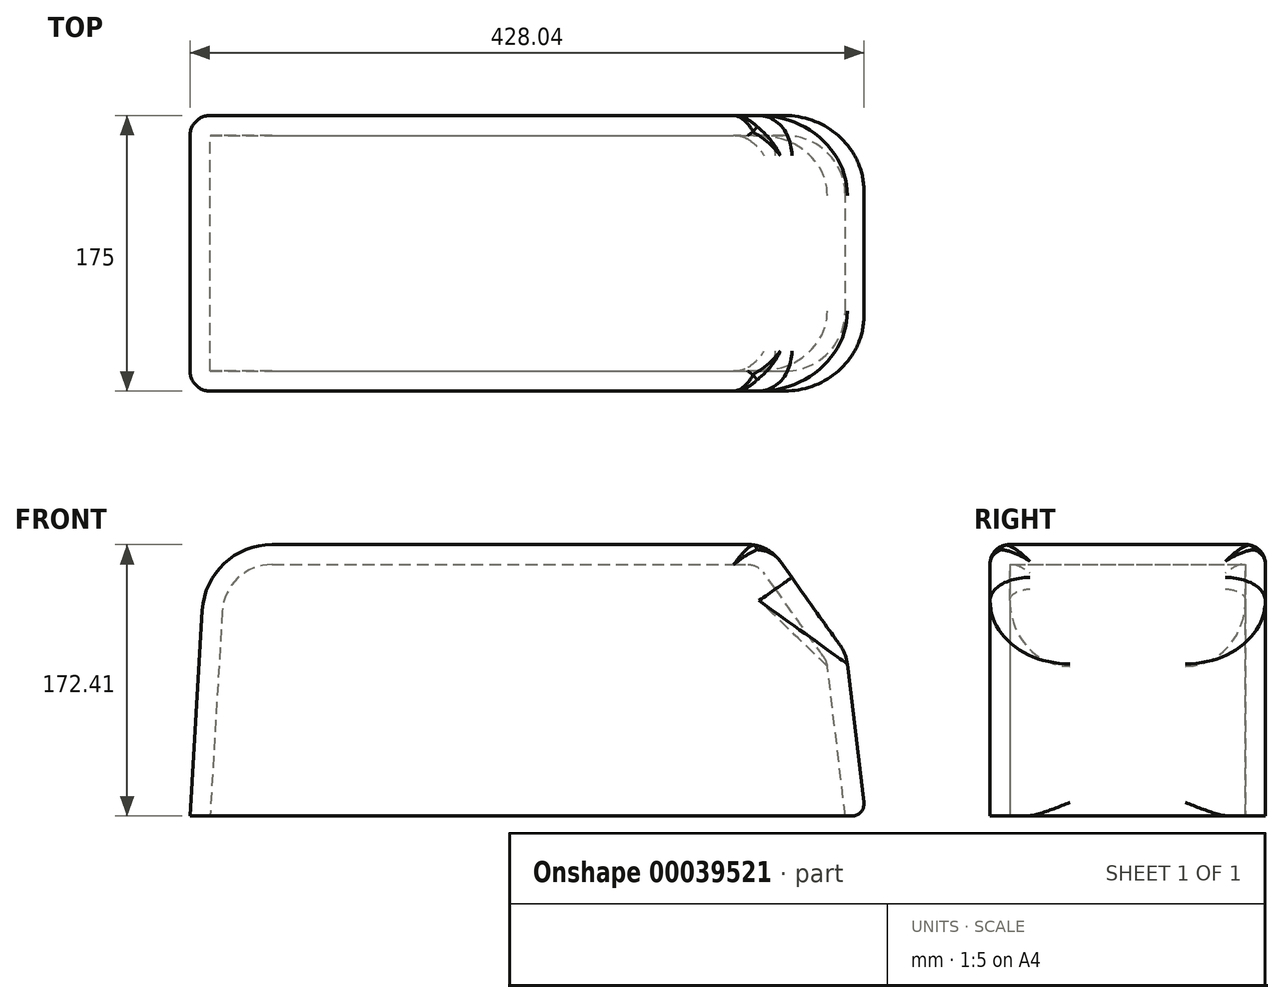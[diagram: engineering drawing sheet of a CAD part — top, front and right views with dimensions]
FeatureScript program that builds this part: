
annotation { "Feature Type Name" : "Feature", "Feature Type Description" : "" }
export const myFeature = defineFeature(function(context is Context, id is Id, definition is map)
    precondition{}
    {
        {
            var Q0;
            Q0=qCreatedBy(makeId("Front.planeOp"),FACE);
            var sketch = newSketch(context, id + "F0", { "sketchPlane" : qUnion([Q0])});
            skPoint(sketch, "E0", {"position": v(0, 0) * mm});
            skPoint(sketch, "E1", {"position": v(-144.5, 0) * mm});
            skPoint(sketch, "E2", {"position": v(95.54, 0) * mm});
            skPoint(sketch, "E3", {"position": v(-169.9, 0) * mm});
            skPoint(sketch, "E4", {"position": v(-119.1, 0) * mm});
            skPoint(sketch, "E5", {"position": v(70.14, 0) * mm});
            skPoint(sketch, "E6", {"position": v(120.94, 0) * mm});
            skLineSegment(sketch, "E7", {"start": v(-213.07, 0) * mm, "end": v(-205.3, 130.6) * mm});
            skLineSegment(sketch, "E8", {"start": v(-213.07, 0) * mm, "end": v(-169.9, 0) * mm});
            skLineSegment(sketch, "E9", {"start": v(-119.1, 0) * mm, "end": v(70.14, 0) * mm});
            skLineSegment(sketch, "E10", {"start": v(120.94, 0) * mm, "end": v(207.35, 0) * mm});
            skPoint(sketch, "E11", {"position": v(168.44, 0) * mm});
            skLineSegment(sketch, "E12", {"start": v(214.92, 8.52) * mm, "end": v(204.41, 96.5) * mm});
            skLineSegment(sketch, "E13", {"start": v(199.9, 108.2) * mm, "end": v(161.88, 161.72) * mm});
            skLineSegment(sketch, "E14", {"start": v(-160.93, 172.41) * mm, "end": v(141.18, 172.41) * mm});
            skPoint(sketch, "E15.visualSharp", {"position": v(-202.81, 172.41) * mm});
            skArc(sketch, "E15.filletArc", {"start": v(-160.93, 172.41) * mm, "mid": v(-191.41, 160.32) * mm, "end": v(-205.3, 130.6) * mm});
            skPoint(sketch, "E16.visualSharp", {"position": v(215.93, 0) * mm});
            skArc(sketch, "E16.filletArc", {"start": v(207.35, 0) * mm, "mid": v(213.05, 2.56) * mm, "end": v(214.92, 8.52) * mm});
            skPoint(sketch, "E17.visualSharp", {"position": v(203.64, 102.93) * mm});
            skArc(sketch, "E17.filletArc", {"start": v(204.41, 96.5) * mm, "mid": v(202.89, 102.64) * mm, "end": v(199.9, 108.2) * mm});
            skPoint(sketch, "E18.visualSharp", {"position": v(154.29, 172.41) * mm});
            skArc(sketch, "E18.filletArc", {"start": v(161.88, 161.72) * mm, "mid": v(152.83, 169.58) * mm, "end": v(141.18, 172.41) * mm});
            skLineSegment(sketch, "E19", {"start": v(-169.9, 0) * mm, "end": v(-119.1, 0) * mm});
            skLineSegment(sketch, "E20", {"start": v(70.14, 0) * mm, "end": v(120.94, 0) * mm});
            skSolve(sketch);
        }
        {
            var Q0;
            Q0=makeQuery(id+"F0.imprint","IMPRINT",FACE,{"disambiguationData":[TD([[makeQuery(id+"F0.imprint","IMPRINT",EDGE,{"derivedFrom":sQuery(id+"F0.wireOp",EDGE,"E7")}),-1.0]])]});
            extrude(context, id + "F1", {"entities" : qUnion([Q0]), "endBound" : BoundingType.SYMMETRIC, "depth" : 175 * mm});
        }
        {
            var Q0;
            Q0=makeQuery(id+"F1.opExtrude","CAP_EDGE",EDGE,{"disambiguationData":[OSD([sQuery(id+"F0.wireOp",EDGE,"E7")])],"isStart":false});
            var Q1;
            Q1=makeQuery(id+"F1.opExtrude","CAP_EDGE",EDGE,{"disambiguationData":[OSD([sQuery(id+"F0.wireOp",EDGE,"E15.filletArc")])],"isStart":false});
            var Q2;
            Q2=makeQuery(id+"F1.opExtrude","CAP_EDGE",EDGE,{"disambiguationData":[OSD([sQuery(id+"F0.wireOp",EDGE,"E14")])],"isStart":false});
            var Q3;
            Q3=makeQuery(id+"F1.opExtrude","CAP_EDGE",EDGE,{"disambiguationData":[OSD([sQuery(id+"F0.wireOp",EDGE,"E14")])],"isStart":true});
            var Q4;
            Q4=makeQuery(id+"F1.opExtrude","CAP_EDGE",EDGE,{"disambiguationData":[OSD([sQuery(id+"F0.wireOp",EDGE,"E15.filletArc")])],"isStart":true});
            var Q5;
            Q5=makeQuery(id+"F1.opExtrude","CAP_EDGE",EDGE,{"disambiguationData":[OSD([sQuery(id+"F0.wireOp",EDGE,"E7")])],"isStart":true});
            fillet(context, id + "F2", {"entities" : qUnion([Q0, Q1, Q2, Q3, Q4, Q5]), "radius" : 12.7 * mm, "allowEdgeOverflow" : false});
        }
        {
            var Q0;
            Q0=makeQuery(id+"F1.opExtrude","CAP_EDGE",EDGE,{"disambiguationData":[OSD([sQuery(id+"F0.wireOp",EDGE,"E12")])],"isStart":false});
            var Q1;
            Q1=makeQuery(id+"F1.opExtrude","CAP_EDGE",EDGE,{"disambiguationData":[OSD([sQuery(id+"F0.wireOp",EDGE,"E12")])],"isStart":true});
            fillet(context, id + "F3", {"entities" : qUnion([Q0, Q1]), "radius" : 50.8 * mm, "allowEdgeOverflow" : false});
        }
        {
            var Q0;
            Q0=makeQuery(id+"F3.opFillet","BLEND_EDGE",EDGE,{"blendedFrom":[makeQuery(id+"F1.opExtrude","CAP_EDGE",EDGE,{"disambiguationData":[OSD([sQuery(id+"F0.wireOp",EDGE,"E12")])],"isStart":false}),makeQuery(id+"F1.opExtrude","SWEPT_FACE",FACE,{"disambiguationData":[OSD([sQuery(id+"F0.wireOp",EDGE,"E13")])]})],"blendedInto":[makeQuery(id+"F1.opExtrude","SWEPT_FACE",FACE,{"disambiguationData":[OSD([sQuery(id+"F0.wireOp",EDGE,"E13")])]})]});
            var Q1;
            Q1=makeQuery(id+"F3.opFillet","BLEND_EDGE",EDGE,{"blendedFrom":[makeQuery(id+"F1.opExtrude","CAP_EDGE",EDGE,{"disambiguationData":[OSD([sQuery(id+"F0.wireOp",EDGE,"E12")])],"isStart":true}),makeQuery(id+"F1.opExtrude","SWEPT_FACE",FACE,{"disambiguationData":[OSD([sQuery(id+"F0.wireOp",EDGE,"E13")])]})],"blendedInto":[makeQuery(id+"F1.opExtrude","SWEPT_FACE",FACE,{"disambiguationData":[OSD([sQuery(id+"F0.wireOp",EDGE,"E13")])]})]});
            fillet(context, id + "F4", {"entities" : qUnion([Q0, Q1]), "radius" : 25.4 * mm, "allowEdgeOverflow" : false});
        }
        {
            var Q0;
            {var subQ0=sQuery(id+"F0.wireOp",EDGE,"E14");Q0=makeQuery(id+"F4.opFillet","BLEND_EDGE",EDGE,{"blendedFrom":[makeQuery(id+"F3.opFillet","BLEND_EDGE",EDGE,{"blendedFrom":[makeQuery(id+"F1.opExtrude","CAP_EDGE",EDGE,{"disambiguationData":[OSD([sQuery(id+"F0.wireOp",EDGE,"E12")])],"isStart":false}),makeQuery(id+"F1.opExtrude","SWEPT_FACE",FACE,{"disambiguationData":[OSD([sQuery(id+"F0.wireOp",EDGE,"E13")])]})],"blendedInto":[makeQuery(id+"F1.opExtrude","SWEPT_FACE",FACE,{"disambiguationData":[OSD([sQuery(id+"F0.wireOp",EDGE,"E13")])]})]}),makeQuery(id+"F2.opFillet","BLEND_FACE",FACE,{"disambiguationData":[OSD([subQ0]),TDD([makeQuery(id+"F1.opExtrude","CAP_EDGE",EDGE,{"disambiguationData":[OSD([subQ0])],"isStart":false})])]})],"blendedInto":[makeQuery(id+"F2.opFillet","BLEND_FACE",FACE,{"disambiguationData":[OSD([subQ0]),TDD([makeQuery(id+"F1.opExtrude","CAP_EDGE",EDGE,{"disambiguationData":[OSD([subQ0])],"isStart":false})])]})]});}
            var Q1;
            Q1=makeQuery(id+"F4.opFillet","BLEND_EDGE",EDGE,{"blendedFrom":[makeQuery(id+"F3.opFillet","BLEND_EDGE",EDGE,{"blendedFrom":[makeQuery(id+"F1.opExtrude","CAP_EDGE",EDGE,{"disambiguationData":[OSD([sQuery(id+"F0.wireOp",EDGE,"E12")])],"isStart":false}),makeQuery(id+"F1.opExtrude","SWEPT_FACE",FACE,{"disambiguationData":[OSD([sQuery(id+"F0.wireOp",EDGE,"E13")])]})],"blendedInto":[makeQuery(id+"F1.opExtrude","SWEPT_FACE",FACE,{"disambiguationData":[OSD([sQuery(id+"F0.wireOp",EDGE,"E13")])]})]}),makeQuery(id+"F1.opExtrude","SWEPT_FACE",FACE,{"disambiguationData":[OSD([sQuery(id+"F0.wireOp",EDGE,"E18.filletArc")])]})],"blendedInto":[makeQuery(id+"F1.opExtrude","SWEPT_FACE",FACE,{"disambiguationData":[OSD([sQuery(id+"F0.wireOp",EDGE,"E18.filletArc")])]})]});
            var Q2;
            Q2=makeQuery(id+"F4.opFillet","BLEND_EDGE",EDGE,{"blendedFrom":[makeQuery(id+"F3.opFillet","BLEND_EDGE",EDGE,{"blendedFrom":[makeQuery(id+"F1.opExtrude","CAP_EDGE",EDGE,{"disambiguationData":[OSD([sQuery(id+"F0.wireOp",EDGE,"E12")])],"isStart":true}),makeQuery(id+"F1.opExtrude","SWEPT_FACE",FACE,{"disambiguationData":[OSD([sQuery(id+"F0.wireOp",EDGE,"E13")])]})],"blendedInto":[makeQuery(id+"F1.opExtrude","SWEPT_FACE",FACE,{"disambiguationData":[OSD([sQuery(id+"F0.wireOp",EDGE,"E13")])]})]}),makeQuery(id+"F1.opExtrude","SWEPT_FACE",FACE,{"disambiguationData":[OSD([sQuery(id+"F0.wireOp",EDGE,"E18.filletArc")])]})],"blendedInto":[makeQuery(id+"F1.opExtrude","SWEPT_FACE",FACE,{"disambiguationData":[OSD([sQuery(id+"F0.wireOp",EDGE,"E18.filletArc")])]})]});
            var Q3;
            {var subQ0=sQuery(id+"F0.wireOp",EDGE,"E14");Q3=makeQuery(id+"F4.opFillet","BLEND_EDGE",EDGE,{"blendedFrom":[makeQuery(id+"F3.opFillet","BLEND_EDGE",EDGE,{"blendedFrom":[makeQuery(id+"F1.opExtrude","CAP_EDGE",EDGE,{"disambiguationData":[OSD([sQuery(id+"F0.wireOp",EDGE,"E12")])],"isStart":true}),makeQuery(id+"F1.opExtrude","SWEPT_FACE",FACE,{"disambiguationData":[OSD([sQuery(id+"F0.wireOp",EDGE,"E13")])]})],"blendedInto":[makeQuery(id+"F1.opExtrude","SWEPT_FACE",FACE,{"disambiguationData":[OSD([sQuery(id+"F0.wireOp",EDGE,"E13")])]})]}),makeQuery(id+"F2.opFillet","BLEND_FACE",FACE,{"disambiguationData":[OSD([subQ0]),TDD([makeQuery(id+"F1.opExtrude","CAP_EDGE",EDGE,{"disambiguationData":[OSD([subQ0])],"isStart":true})])]})],"blendedInto":[makeQuery(id+"F2.opFillet","BLEND_FACE",FACE,{"disambiguationData":[OSD([subQ0]),TDD([makeQuery(id+"F1.opExtrude","CAP_EDGE",EDGE,{"disambiguationData":[OSD([subQ0])],"isStart":true})])]})]});}
            fillet(context, id + "F5", {"entities" : qUnion([Q0, Q1, Q2, Q3]), "radius" : 5.08 * mm, "tangentPropagation" : true, "allowEdgeOverflow" : false});
        }
        {
            var Q0;
            Q0=makeQuery(id+"F1.opExtrude","SWEPT_FACE",FACE,{"disambiguationData":[OSD([sQuery(id+"F0.wireOp",EDGE,"E8"),sQuery(id+"F0.wireOp",EDGE,"E9"),sQuery(id+"F0.wireOp",EDGE,"E10"),sQuery(id+"F0.wireOp",EDGE,"E19"),sQuery(id+"F0.wireOp",EDGE,"E20")])]});
            shell(context, id + "F6", {"entities" : qUnion([Q0]), "thickness" : 12.7 * mm});
        }
    });
